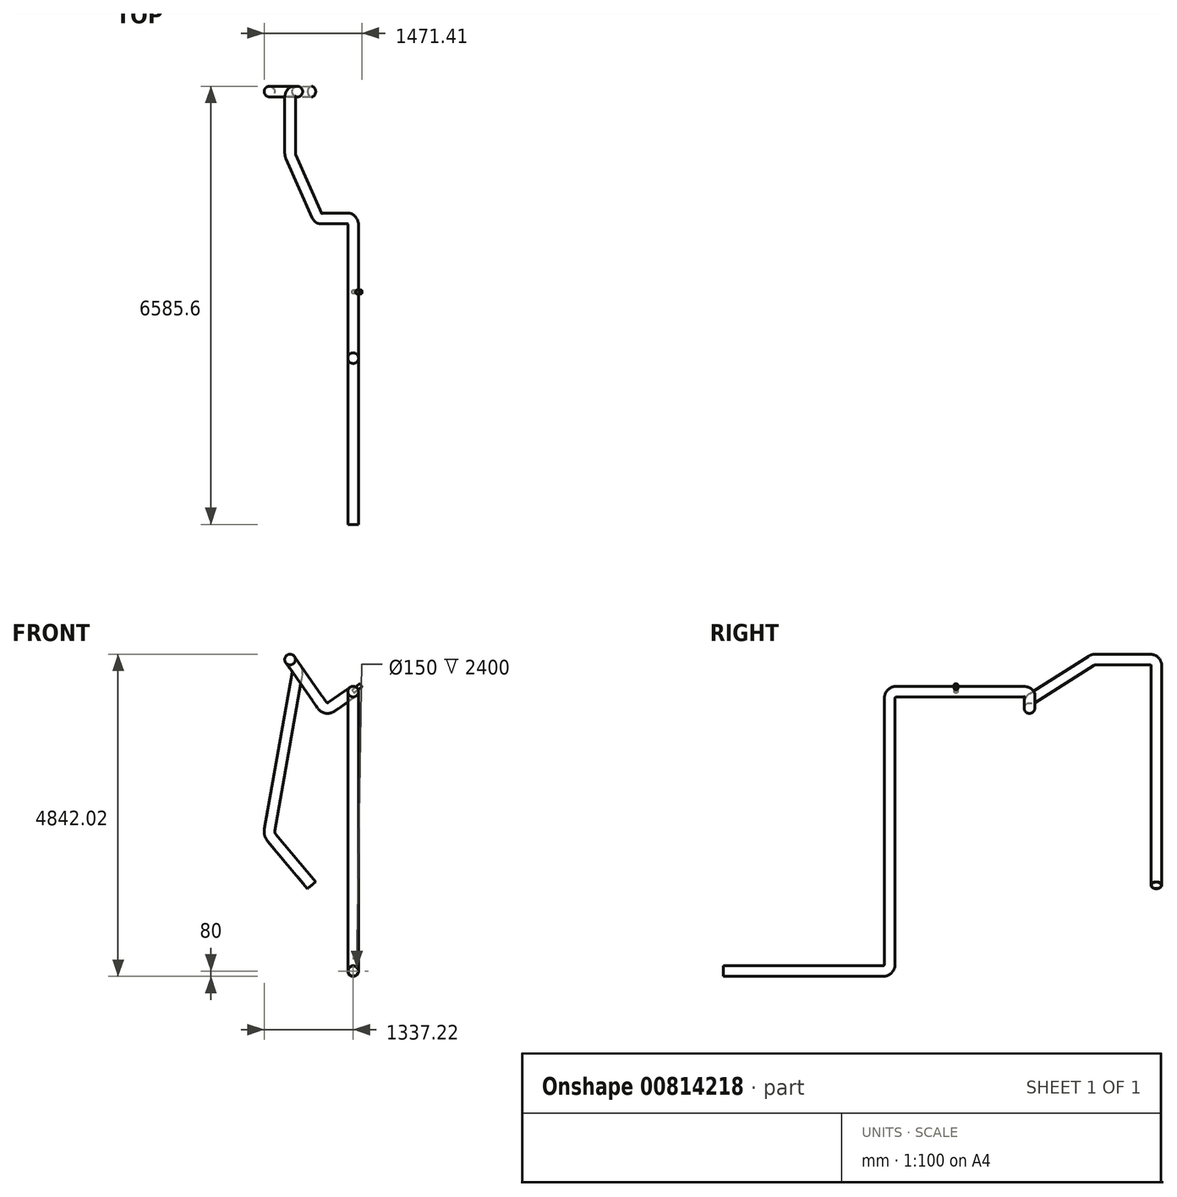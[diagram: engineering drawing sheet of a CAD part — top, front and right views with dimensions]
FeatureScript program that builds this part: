
annotation { "Feature Type Name" : "Feature", "Feature Type Description" : "" }
export const myFeature = defineFeature(function(context is Context, id is Id, definition is map)
    precondition{}
    {
        {
            var Q0;
            Q0=qCreatedBy(makeId("Front.planeOp"),FACE);
            var sketch = newSketch(context, id + "F0", { "sketchPlane" : qUnion([Q0])});
            skCircle(sketch, "E0", {"center": v(0, 0) * mm, "radius": 80 * mm});
            skCircle(sketch, "E1", {"center": v(0, 0) * mm, "radius": 75 * mm});
            skSolve(sketch);
        }
        {
            var Q0;
            Q0=qCreatedBy(makeId("Right.planeOp"),FACE);
            var sketch = newSketch(context, id + "F1", { "sketchPlane" : qUnion([Q0])});
            skLineSegment(sketch, "E2", {"start": v(0, 0) * mm, "end": v(2400, 0) * mm});
            skLineSegment(sketch, "E3", {"start": v(2500, 100) * mm, "end": v(2500, 4100) * mm});
            skPoint(sketch, "E4.visualSharp", {"position": v(2500, 4000) * mm});
            skArc(sketch, "E4.filletArc", {"start": v(2505, 5000) * mm, "mid": v(2501.46, 4998.54) * mm, "end": v(2500, 4995) * mm});
            skArc(sketch, "E5.filletArc", {"start": v(2600, 4200) * mm, "mid": v(2529.29, 4170.71) * mm, "end": v(2500, 4100) * mm});
            skPoint(sketch, "E6.visualSharp", {"position": v(2500, 0) * mm});
            skArc(sketch, "E6.filletArc", {"start": v(2400, 0) * mm, "mid": v(2470.71, 29.29) * mm, "end": v(2500, 100) * mm});
            skLineSegment(sketch, "E7", {"start": v(2600, 4200) * mm, "end": v(4600, 4200) * mm});
            skSolve(sketch);
        }
        {
            var Q0;
            Q0=sQuery(id+"F1.wireOp",VERTEX,"E7.end");
            var Q1;
            Q1=qCreatedBy(makeId("Front.planeOp"),FACE);
            cPlane(context, id + "F2", {"entities" : qUnion([Q0, Q1]), "cplaneType" : CPlaneType.PLANE_POINT, "offset" : 25 * mm, "width" : 150 * mm, "height" : 150 * mm});
        }
        {
            var Q0;
            Q0=qCreatedBy(makeId("Top.planeOp"),FACE);
            var Q1;
            Q1=sQuery(id+"F1.wireOp",VERTEX,"E7.end");
            cPlane(context, id + "F3", {"entities" : qUnion([Q0, Q1]), "cplaneType" : CPlaneType.PLANE_POINT, "offset" : 25 * mm, "width" : 150 * mm, "height" : 150 * mm});
        }
        {
            var Q0;
            Q0=qCreatedBy(id+"F3.planeOp",FACE);
            var Q1;
            Q1=sQuery(id+"F1.wireOp",EDGE,"E7");
            cPlane(context, id + "F4", {"entities" : qUnion([Q0, Q1]), "cplaneType" : CPlaneType.LINE_ANGLE, "offset" : 25 * mm, "angle" : 145 * degree, "width" : 150 * mm, "height" : 150 * mm});
        }
        {
            var Q0;
            Q0=qCreatedBy(id+"F4.planeOp",FACE);
            var sketch = newSketch(context, id + "F5", { "sketchPlane" : qUnion([Q0])});
            skLineSegment(sketch, "E8.0", {"start": v(2409.02, 2600) * mm, "end": v(2409.02, 4500) * mm});
            skLineSegment(sketch, "E9", {"start": v(2309.02, 4600) * mm, "end": v(1909.02, 4600) * mm});
            skPoint(sketch, "E10.visualSharp", {"position": v(2409.02, 4600) * mm});
            skArc(sketch, "E10.filletArc", {"start": v(2409.02, 4500) * mm, "mid": v(2379.73, 4570.71) * mm, "end": v(2309.02, 4600) * mm});
            skSolve(sketch);
        }
        {
            var Q0;
            Q0=qCreatedBy(id+"F2.planeOp",FACE);
            var Q1;
            Q1=sQuery(id+"F5.wireOp",VERTEX,"E9.end");
            cPlane(context, id + "F6", {"entities" : qUnion([Q0, Q1]), "cplaneType" : CPlaneType.PLANE_POINT, "offset" : 25 * mm, "width" : 150 * mm, "height" : 150 * mm});
        }
        {
            var Q0;
            Q0=qCreatedBy(id+"F6.planeOp",FACE);
            var sketch = newSketch(context, id + "F7", { "sketchPlane" : qUnion([Q0])});
            skLineSegment(sketch, "E11.0", {"start": v(-81.92, 4142.64) * mm, "end": v(-327.66, 3970.57) * mm});
            skLineSegment(sketch, "E12", {"start": v(-466.93, 3995.13) * mm, "end": v(-524.3, 4077.04) * mm});
            skPoint(sketch, "E13.visualSharp", {"position": v(-409.58, 3913.21) * mm});
            skArc(sketch, "E13.filletArc", {"start": v(-466.93, 3995.13) * mm, "mid": v(-402.38, 3954) * mm, "end": v(-327.66, 3970.57) * mm});
            skSolve(sketch);
        }
        {
            var Q0;
            Q0=sQuery(id+"F7.wireOp",VERTEX,"E11.0.end");
            var Q1;
            Q1=sQuery(id+"F7.wireOp",VERTEX,"E12.start");
            var Q2;
            Q2=sQuery(id+"F7.wireOp",VERTEX,"E12.end");
            cPlane(context, id + "F8", {"entities" : qUnion([Q0, Q1, Q2]), "cplaneType" : CPlaneType.THREE_POINT, "offset" : 25 * mm, "width" : 150 * mm, "height" : 150 * mm});
        }
        {
            var Q0;
            Q0=qCreatedBy(id+"F8.planeOp",FACE);
            var Q1;
            Q1=sQuery(id+"F7.wireOp",EDGE,"E12");
            cPlane(context, id + "F9", {"entities" : qUnion([Q0, Q1]), "cplaneType" : CPlaneType.LINE_ANGLE, "offset" : 25 * mm, "angle" : 90 * degree, "width" : 150 * mm, "height" : 150 * mm});
        }
        {
            var Q0;
            Q0=qCreatedBy(id+"F9.planeOp",FACE);
            var sketch = newSketch(context, id + "F10", { "sketchPlane" : qUnion([Q0])});
            skLineSegment(sketch, "E14.0", {"start": v(-4600, 3540.44) * mm, "end": v(-4600, 3591.37) * mm});
            skLineSegment(sketch, "E15", {"start": v(-4638.81, 3670.46) * mm, "end": v(-5527.61, 4358.08) * mm});
            skLineSegment(sketch, "E16", {"start": v(-5588.8, 4378.98) * mm, "end": v(-6405.6, 4378.98) * mm});
            skPoint(sketch, "E17.visualSharp", {"position": v(-4600, 3640.44) * mm});
            skArc(sketch, "E17.filletArc", {"start": v(-4600, 3591.37) * mm, "mid": v(-4610.23, 3635.42) * mm, "end": v(-4638.81, 3670.46) * mm});
            skPoint(sketch, "E18.visualSharp", {"position": v(-5554.64, 4378.98) * mm});
            skArc(sketch, "E18.filletArc", {"start": v(-5527.61, 4358.08) * mm, "mid": v(-5556.47, 4373.61) * mm, "end": v(-5588.8, 4378.98) * mm});
            skPoint(sketch, "E19.visualSharp", {"position": v(-6505.6, 4378.98) * mm});
            skLineSegment(sketch, "E20", {"start": v(-6505.6, 4278.98) * mm, "end": v(-6505.6, 4178.6) * mm});
            skArc(sketch, "E21.filletArc", {"start": v(-6405.6, 4378.98) * mm, "mid": v(-6476.3, 4349.7) * mm, "end": v(-6505.6, 4278.98) * mm});
            skSolve(sketch);
        }
        {
            var Q0;
            Q0=qCreatedBy(id+"F6.planeOp",FACE);
            var Q1;
            Q1=sQuery(id+"F10.wireOp",VERTEX,"E20.end");
            cPlane(context, id + "F11", {"entities" : qUnion([Q0, Q1]), "cplaneType" : CPlaneType.PLANE_POINT, "offset" : 25 * mm, "width" : 150 * mm, "height" : 150 * mm});
        }
        {
            var Q0;
            Q0=qCreatedBy(id+"F11.planeOp",FACE);
            var sketch = newSketch(context, id + "F12", { "sketchPlane" : qUnion([Q0])});
            skLineSegment(sketch, "E22.0", {"start": v(-890.55, 4600.1) * mm, "end": v(-856.72, 4551.8) * mm});
            skLineSegment(sketch, "E23", {"start": v(-840.16, 4477.08) * mm, "end": v(-1254.94, 2124.73) * mm});
            skPoint(sketch, "E24.visualSharp", {"position": v(-832.96, 4517.87) * mm});
            skArc(sketch, "E24.filletArc", {"start": v(-840.16, 4477.08) * mm, "mid": v(-841, 4516.09) * mm, "end": v(-856.72, 4551.8) * mm});
            skLineSegment(sketch, "E25", {"start": v(-1222.12, 2002.27) * mm, "end": v(-624.3, 1289.8) * mm});
            skPoint(sketch, "E26.visualSharp", {"position": v(-1267.08, 2055.85) * mm});
            skArc(sketch, "E26.filletArc", {"start": v(-1254.94, 2124.73) * mm, "mid": v(-1252.1, 2059.86) * mm, "end": v(-1222.12, 2002.27) * mm});
            skSolve(sketch);
        }
        {
            var Q0;
            Q0=makeQuery(id+"F0.imprint","IMPRINT",FACE,{"disambiguationData":[TD([[makeQuery(id+"F0.imprint","IMPRINT",EDGE,{"derivedFrom":sQuery(id+"F0.wireOp",EDGE,"E0")}),1.0]])]});
            var Q1;
            Q1=sQuery(id+"F1.wireOp",EDGE,"E2");
            var Q2;
            Q2=sQuery(id+"F1.wireOp",EDGE,"E6.filletArc");
            var Q3;
            Q3=sQuery(id+"F1.wireOp",EDGE,"E3");
            var Q4;
            Q4=sQuery(id+"F1.wireOp",EDGE,"E5.filletArc");
            var Q5;
            Q5=sQuery(id+"F5.wireOp",EDGE,"E8.0");
            var Q6;
            Q6=sQuery(id+"F5.wireOp",EDGE,"E10.filletArc");
            var Q7;
            Q7=sQuery(id+"F7.wireOp",EDGE,"E11.0");
            var Q8;
            Q8=sQuery(id+"F7.wireOp",EDGE,"E13.filletArc");
            var Q9;
            Q9=sQuery(id+"F10.wireOp",EDGE,"E14.0");
            var Q10;
            Q10=sQuery(id+"F10.wireOp",EDGE,"E17.filletArc");
            var Q11;
            Q11=sQuery(id+"F10.wireOp",EDGE,"E15");
            var Q12;
            Q12=sQuery(id+"F10.wireOp",EDGE,"E18.filletArc");
            var Q13;
            Q13=sQuery(id+"F10.wireOp",EDGE,"E16");
            var Q14;
            Q14=sQuery(id+"F10.wireOp",EDGE,"E21.filletArc");
            var Q15;
            Q15=sQuery(id+"F12.wireOp",EDGE,"E22.0");
            var Q16;
            Q16=sQuery(id+"F12.wireOp",EDGE,"E24.filletArc");
            var Q17;
            Q17=sQuery(id+"F12.wireOp",EDGE,"E23");
            var Q18;
            Q18=sQuery(id+"F12.wireOp",EDGE,"E26.filletArc");
            var Q19;
            Q19=sQuery(id+"F12.wireOp",EDGE,"E25");
            sweep(context, id + "F13", {"profiles" : qUnion([Q0]), "path" : qUnion([Q1, Q2, Q3, Q4, Q5, Q6, Q7, Q8, Q9, Q10, Q11, Q12, Q13, Q14, Q15, Q16, Q17, Q18, Q19])});
        }
        {
            var Q0;
            Q0=makeQuery(id+"F13.opSweep","SWEPT_FACE",FACE,{"disambiguationData":[OSD([sQuery(id+"F0.wireOp",EDGE,"E0"),sQuery(id+"F5.wireOp",EDGE,"E8.0")])]});
            cPlane(context, id + "F14", {"entities" : qUnion([Q0]), "cplaneType" : CPlaneType.LINE_ANGLE, "offset" : 25 * mm, "angle" : 130 * degree, "oppositeDirection" : true, "width" : 150 * mm, "height" : 150 * mm});
        }
        {
            var Q0;
            Q0=qCreatedBy(id+"F14.planeOp",FACE);
            var sketch = newSketch(context, id + "F15", { "sketchPlane" : qUnion([Q0])});
            skCircle(sketch, "E27", {"center": v(-3495.35, 3217.39) * mm, "radius": 30 * mm});
            skLineSegment(sketch, "E28", {"start": v(-2600, 3137.39) * mm, "end": v(-4500, 3137.39) * mm});
            skLineSegment(sketch, "E29", {"start": v(-4500, 3297.39) * mm, "end": v(-2600, 3297.39) * mm});
            skCircle(sketch, "E30", {"center": v(-3495.35, 3217.39) * mm, "radius": 25 * mm});
            skSolve(sketch);
        }
        {
            var Q0;
            Q0 = qSketchRegion(id + "F15", true);
            extrude(context, id + "F16", {"entities" : qUnion([Q0]), "operationType" : NewBodyOperationType.ADD, "oppositeDirection" : true, "depth" : 150 * mm, "offsetDistance" : 25 * mm});
        }
    });
